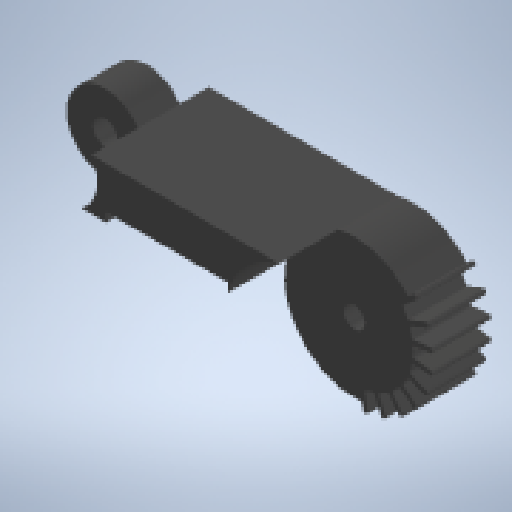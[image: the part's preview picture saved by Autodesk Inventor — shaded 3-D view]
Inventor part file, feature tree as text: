
AUTODESK INVENTOR PART (.ipt)
format: ipt  version: 2025.2 (Build 292293000, 293)  size: 268,288 bytes
history: native  units: mm
features: sketch x5, other x4
ambient origin geometry x8: Origin, YZ Plane, XZ Plane, XY Plane, X Axis, Y Axis, Z Axis, Center Point
bodies: Body1 (feature_tree)
feature tree (9):
  other  "Engrenagem2_0001_001.ipt"
  other  "Sólido1::Engrenagem2_0001_001.ipt"
  other  "OperaçãoIdentificador1"
  sketch  "Esboço1"  dims[d0=10.0mm]
  sketch  "Esboço2"
  sketch  "Esboço3"
  sketch  "Esboço4"
  sketch  "Esboço5"
  other  "Sólido1"
